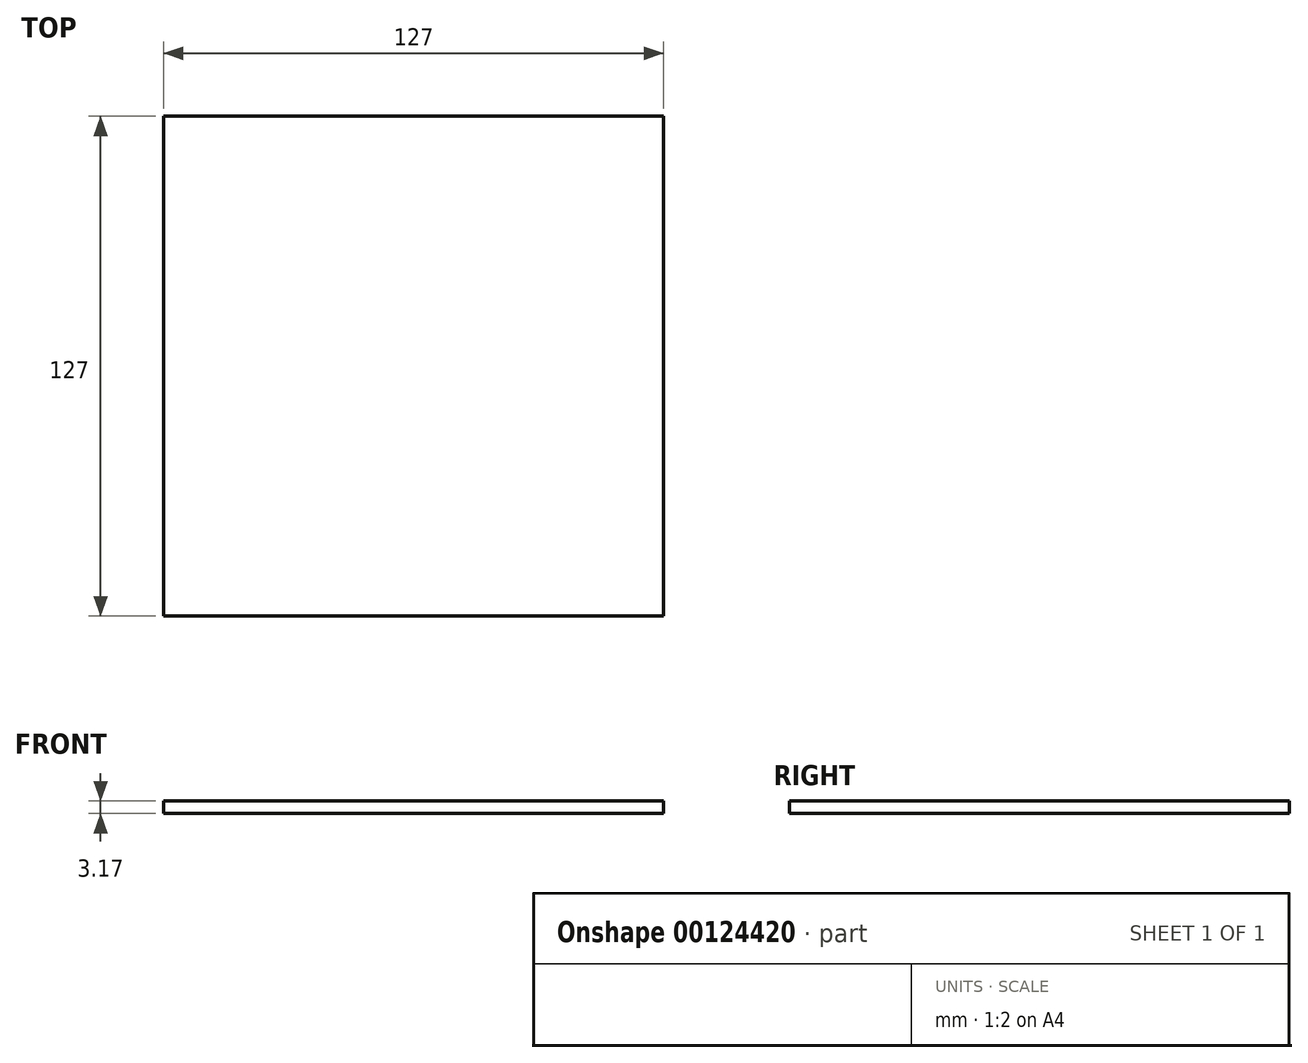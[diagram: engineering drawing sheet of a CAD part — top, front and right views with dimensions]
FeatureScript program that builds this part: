
annotation { "Feature Type Name" : "Feature", "Feature Type Description" : "" }
export const myFeature = defineFeature(function(context is Context, id is Id, definition is map)
    precondition{}
    {
        {
            var Q0;
            Q0=qCreatedBy(makeId("Top.planeOp"),FACE);
            var sketch = newSketch(context, id + "F0", { "sketchPlane" : qUnion([Q0])});
            skLineSegment(sketch, "E0.bottom", {"start": v(63.5, -63.5) * mm, "end": v(-63.5, -63.5) * mm});
            skLineSegment(sketch, "E0.top", {"start": v(63.5, 63.5) * mm, "end": v(-63.5, 63.5) * mm});
            skLineSegment(sketch, "E0.left", {"start": v(63.5, -63.5) * mm, "end": v(63.5, 63.5) * mm});
            skLineSegment(sketch, "E0.right", {"start": v(-63.5, -63.5) * mm, "end": v(-63.5, 63.5) * mm});
            skPoint(sketch, "E0.middle", {"position": v(0, 0) * mm});
            skSolve(sketch);
        }
        {
            var Q0;
            Q0 = qSketchRegion(id + "F0", true);
            extrude(context, id + "F1", {"entities" : qUnion([Q0]), "depth" : 3.17 * mm});
        }
    });
